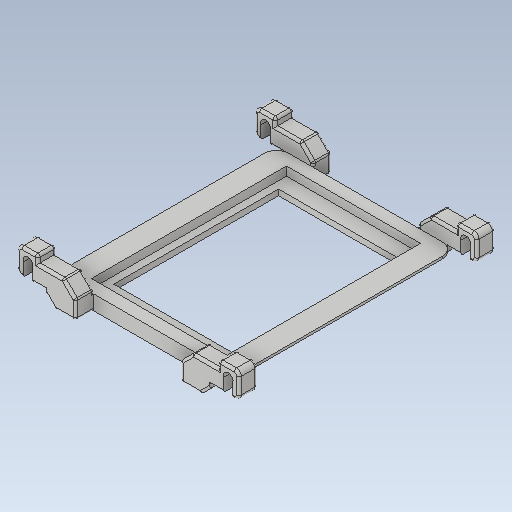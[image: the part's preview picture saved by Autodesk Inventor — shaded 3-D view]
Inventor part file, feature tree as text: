
AUTODESK INVENTOR PART (.ipt)
format: ipt  version: 2020 (Build 240168000, 168)  size: 473,600 bytes
history: native  units: in
note: dims shown in document units (in); Inventor stores cm internally (conversion verified against a paired STEP export)
features: projected_geometry x13, extrude x12, sketch x12, fillet x4, plane x4, mirror x4
ambient origin geometry x8: Origin, YZ Plane, XZ Plane, XY Plane, X Axis, Y Axis, Z Axis, Center Point
bodies: Solid1 (feature_tree)
feature tree (49):
  extrude  "Extrusion1"  Depth=7.0866in
  extrude  "Extrusion2"  Depth=0.2835in TaperAngle=0.0deg
  extrude  "Extrusion3"  Depth=4.3307in
  fillet  "Fillet1"  Radius=6.2992in
  plane  "Work Plane4"
  extrude  "Extrusion8"  Depth=3.8661in
  sketch  "Sketch9"  dims[d21=0.6299in d23=0.6338in]
  plane  "Work Plane1"
  extrude  "Extrusion4"  [1 undecoded]
  extrude  "Extrusion5"  Depth=0.3228in
  extrude  "Extrusion9"  Depth=0.315in
  extrude  "Extrusion10"  Depth=0.6338in
  extrude  "Extrusion11"  Depth=0.9843in
  extrude  "Extrusion12"  [1 undecoded]
  fillet  "Fillet2"  Radius=1.8898in
  fillet  "Fillet4"  Radius=0.3228in
  fillet  "Fillet5"  Radius=0.3543in
  plane  "Work Plane2"
  plane  "Work Plane3"
  extrude  "Extrusion13"  Depth=1.2243in
  mirror  "Mirror3"
  mirror  "Mirror4"
  mirror  "Mirror1"
  mirror  "Mirror2"
  extrude  "Extrusion7"  Depth=0.0394in TaperAngle=0.0deg
  sketch  "Sketch1"  dims[d0=5.7559in d1=7.0866in]
  sketch  "Sketch2"  dims[d2=0.4724in d3=0.0in d4=0.2835in d5=0.0in]
  sketch  "Sketch3"  dims[d6=0.1969in d7=0.0in d8=4.3307in d9=6.2992in]
  sketch  "Sketch4"  dims[d10=5.3228in d11=3.8661in]
  projected_geometry  "Projected Loop1"
  projected_geometry  "Projected Loop2"
  projected_geometry  "Projected Loop3"
  sketch  "Sketch5"  dims[d12=0.3937in d13=-1.1811in]
  sketch  "Sketch7"  dims[d14=0.7874in d15=0.0in d16=0.3228in]
  projected_geometry  "Projected Loop7"
  projected_geometry  "Projected Loop8"
  sketch  "Sketch8"  dims[d17=0.7874in d18=0.0in d20=0.315in]
  projected_geometry  "Projected Loop9"
  projected_geometry  "Projected Loop10"
  projected_geometry  "Projected Loop11"
  sketch  "Sketch10"  dims[d24=0.9843in d28=0.4331in]
  projected_geometry  "Projected Loop12"
  sketch  "Sketch11"  dims[d29=3.937in d30=0.0in d31=-1.1811in d32=1.8898in d33=0.0in d34=0.3228in d35=0.3543in]
  projected_geometry  "Projected Loop13"
  projected_geometry  "Projected Loop14"
  sketch  "Sketch12"  dims[d36=0.87in d37=1.2243in]
  projected_geometry  "Projected Loop15"
  sketch  "Sketch13"  dims[d38=0.5906in d39=2.3622in d40=0.0in d41=0.9449in d42=0.3937in d43=2.3622in d44=0.0in d45=0.1575in d47=0.0787in d48=0.2362in d49=2.3622in d50=0.0in d51=45.0deg d52=0.3937in d53=2.3622in d54=0.0in d55=0.2756in d56=0.0787in d57=0.0079in d58=0.0079in d59=2.3622in d60=0.0in d61=0.0394in]
  projected_geometry  "Projected Loop16"
note: 2 required parameter values undecoded (feature->parameter linkage not recoverable at this tier; creation-order binding heuristic only, values carry confidence <= 0.55)
